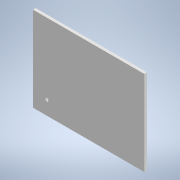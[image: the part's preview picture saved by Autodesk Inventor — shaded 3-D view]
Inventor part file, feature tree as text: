
AUTODESK INVENTOR PART (.ipt)
format: ipt  version: 2020 (Build 240168000, 168)  size: 92,672 bytes
history: native  units: in
note: dims shown in document units (in); Inventor stores cm internally (conversion verified against a paired STEP export)
features: other x3, extrude x1, sketch x1, reference x1
ambient origin geometry x8: Origin, YZ Plane, XZ Plane, XY Plane, X Axis, Y Axis, Z Axis, Center Point
bodies: Solid1 (feature_tree)
feature tree (6):
  extrude  "Extrusion1"  Depth=0.1in
  sketch  "Sketch1"  dims[d0=0.5in d1=0.5in d2=0.5in d3=0.5in d4=0.1in d5=0.0in]
  reference  "Reference1"
  other  "<userpath>\Documents\Inventor\Drone\OdroidParts\OdroidAssembly.iam"
  other  "OdroidAssembly.iam"
  other  "odroidstandoff:4"
